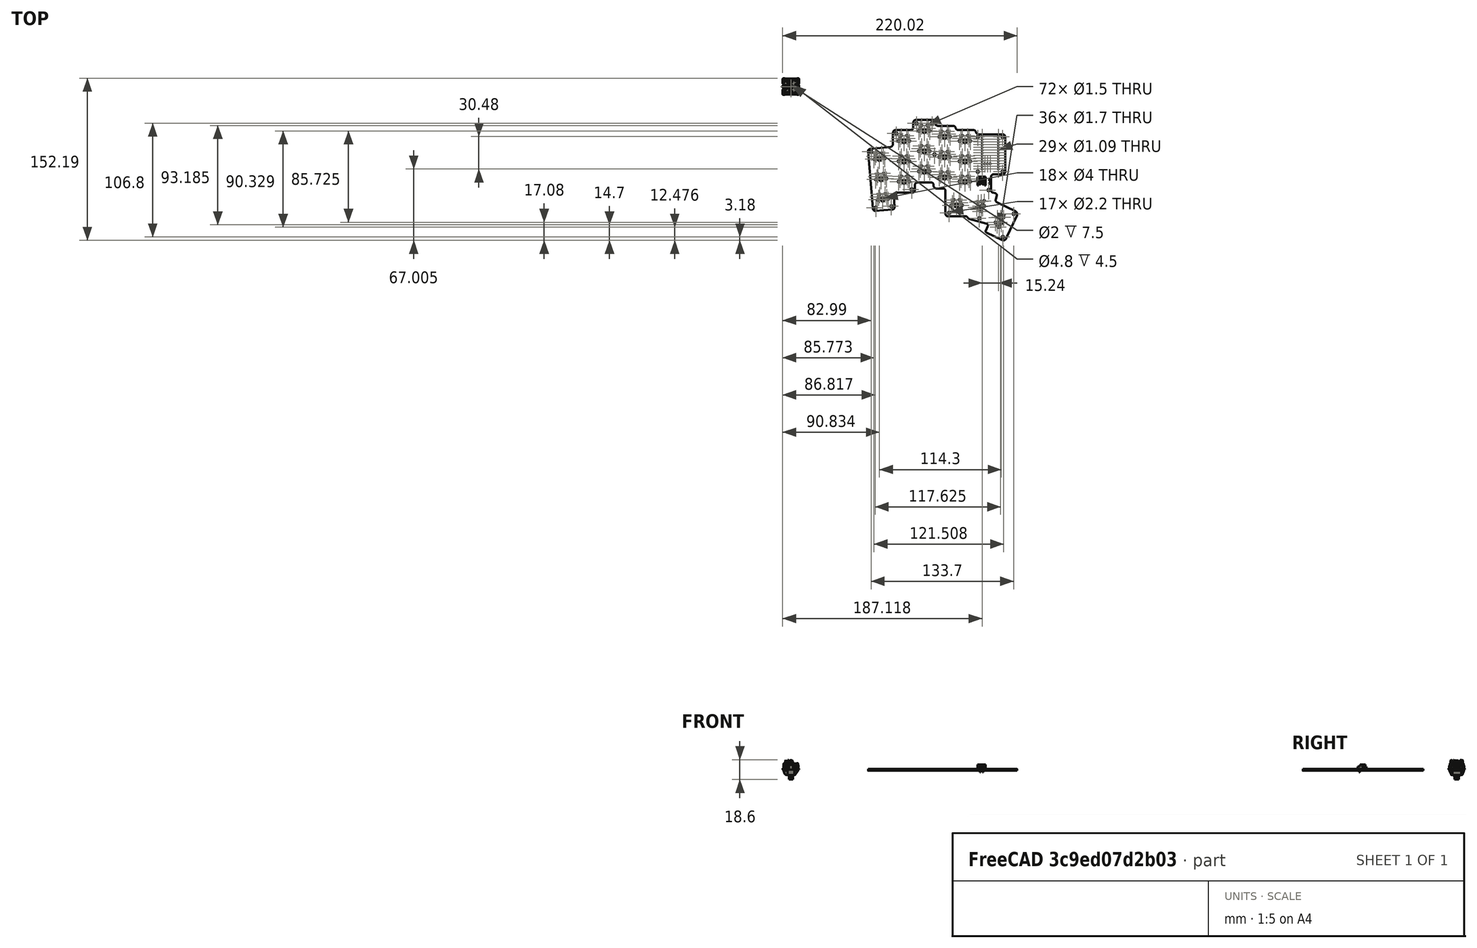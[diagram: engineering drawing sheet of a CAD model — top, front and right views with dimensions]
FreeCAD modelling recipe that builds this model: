
FCSTD DOCUMENT  (FreeCAD 0.19R24267 +99 (Git))
Label: Diom-35SP
License: All rights reserved
LicenseURL: http://en.wikipedia.org/wiki/All_rights_reserved
objects: App::Link×17, Part::Feature×12, App::Part×5, PartDesign::CoordinateSystem×1, Sketcher::SketchObject×1
note: 14 computed .brp shape members not serialized (recipe doc carries the construction recipe); baked Part::Feature solids carry a one-line shape summary decoded from their .brp

FEATURE [PartDesign::CoordinateSystem] Local_CS_b1ef
  AttacherType = Attacher::AttachEngine3D
FEATURE [Part::Feature] Pcb_b1ef
  shape: bbox 139.9 x 113.1 x 1.6 mm, 239 faces (baked)
FEATURE [Sketcher::SketchObject] PCB_Sketch_b1ef
  FullyConstrained = false
  sketch-geometry (61):
    g0: LineSegment StartX=188.042 StartY=-84.455 StartZ=0 EndX=188.019 EndY=-97 EndZ=0
    g1: LineSegment StartX=93.6625 StartY=-56.3562 StartZ=0 EndX=74.7 EndY=-58.2 EndZ=0
    g2: LineSegment StartX=77.1188 StartY=-114.019 StartZ=0 EndX=72.6 EndY=-60.6 EndZ=0
    g3: LineSegment StartX=135.604 StartY=-34.1313 StartZ=0 EndX=135.604 EndY=-33.3375 EndZ=0
    g4: LineSegment StartX=190.423 StartY=-82.042 StartZ=0 EndX=198.882 EndY=-82.042 EndZ=0
    g5: LineSegment StartX=145.256 StartY=-119.412 StartZ=0 EndX=145.256 EndY=-97.282 EndZ=0
    g6: LineSegment StartX=189.8 StartY=-99.3 StartZ=0 EndX=192.1 EndY=-99.9 EndZ=0
    g7: LineSegment StartX=198.882 StartY=-44.45 StartZ=0 EndX=176.213 EndY=-44.45 EndZ=0
    g8: LineSegment StartX=202.4 StartY=-141.9 StartZ=0 EndX=212.306 EndY=-120.437 EndZ=0
    g9: LineSegment StartX=112.713 StartY=-40.4813 StartZ=0 EndX=98.425 EndY=-40.4813 EndZ=0
    g10: LineSegment StartX=119 StartY=-89.7 StartZ=0 EndX=131.762 EndY=-89.6937 EndZ=0
    g11: LineSegment StartX=167.6 StartY=-124 StartZ=0 EndX=183.822 EndY=-128.377 EndZ=0
    g12: LineSegment StartX=183.515 StartY=-136.779 StartZ=0 EndX=198.209 EndY=-143.805 EndZ=0
    g13: LineSegment StartX=210.805 StartY=-116.739 StartZ=0 EndX=193.6 EndY=-108.4 EndZ=0
    g14: LineSegment StartX=116.619 StartY=-92.0812 StartZ=0 EndX=116.6 EndY=-96.8375 EndZ=0
    g15: LineSegment StartX=95.25 StartY=-115.094 StartZ=0 EndX=79.5 EndY=-116.4 EndZ=0
    g16: LineSegment StartX=136.525 StartY=-95.25 StartZ=0 EndX=142.875 EndY=-95.25 EndZ=0
    g17: LineSegment StartX=114.219 StartY=-99.2188 StartZ=0 EndX=99.2188 EndY=-99.2188 EndZ=0
    g18: LineSegment StartX=115.094 StartY=-33.3375 StartZ=0 EndX=115.094 EndY=-38.1 EndZ=0
    g19: LineSegment StartX=201.263 StartY=-46.8312 StartZ=0 EndX=201.263 EndY=-79.6607 EndZ=0
    g20: LineSegment StartX=192.408 StartY=-105.58 StartZ=0 EndX=193.4 EndY=-102.2 EndZ=0
    g21: LineSegment StartX=96.0438 StartY=-42.8625 StartZ=0 EndX=96.0438 EndY=-53.975 EndZ=0
    g22: LineSegment StartX=171.45 StartY=-40.4813 StartZ=0 EndX=157.162 EndY=-40.4813 EndZ=0
    g23: LineSegment StartX=134.144 StartY=-92.075 StartZ=0 EndX=134.144 EndY=-92.8688 EndZ=0
    g24: LineSegment StartX=96.8375 StartY=-101.6 StartZ=0 EndX=97.6312 EndY=-112.713 EndZ=0
    g25: LineSegment StartX=133.223 StartY=-30.9563 StartZ=0 EndX=117.475 EndY=-30.9562 EndZ=0
    g26: LineSegment StartX=152.4 StartY=-36.5125 StartZ=0 EndX=138.004 EndY=-36.5125 EndZ=0
    g27: LineSegment StartX=184.893 StartY=-130.9 StartZ=0 EndX=183.134 EndY=-134.62 EndZ=0
    g28: LineSegment StartX=147.637 StartY=-121.444 StartZ=0 EndX=164.2 EndY=-121.444 EndZ=0
    g29: ArcOfCircle CenterX=133.223 CenterY=-33.3375 CenterZ=0 NormalX=0 NormalY=0 NormalZ=-1 AngleXU=1.5708 Radius=2.38125 StartAngle=0 EndAngle=1.5708
    g30: ArcOfCircle CenterX=209.705 CenterY=-119.339 CenterZ=0 NormalX=0 NormalY=0 NormalZ=-1 AngleXU=1.97104 Radius=2.82312 StartAngle=0 EndAngle=1.57002
    g31: ArcOfCircle CenterX=131.762 CenterY=-92.075 CenterZ=0 NormalX=0 NormalY=0 NormalZ=-1 AngleXU=1.5708 Radius=2.38125 StartAngle=0 EndAngle=1.5708
    g32: ArcOfCircle CenterX=79.5 CenterY=-114.019 CenterZ=0 NormalX=0 NormalY=0 NormalZ=-1 AngleXU=-1.57079 Radius=2.38125 StartAngle=0 EndAngle=1.57079
    g33: ArcOfCircle CenterX=136.525 CenterY=-92.8687 CenterZ=0 NormalX=0 NormalY=0 NormalZ=-1 AngleXU=-1.5708 Radius=2.38125 StartAngle=0 EndAngle=1.5708
    g34: ArcOfCircle CenterX=119 CenterY=-92.0813 CenterZ=0 NormalX=0 NormalY=0 NormalZ=-1 AngleXU=3.25477e-08 Radius=2.38125 StartAngle=0 EndAngle=1.5708
    g35: ArcOfCircle CenterX=164.177 CenterY=-123.544 CenterZ=0 NormalX=0 NormalY=0 NormalZ=-1 AngleXU=1.5819 Radius=2.10035 StartAngle=0 EndAngle=1.14618
    g36: ArcOfCircle CenterX=152.4 CenterY=-38.9238 CenterZ=0 NormalX=0 NormalY=0 NormalZ=-1 AngleXU=1.5708 Radius=2.41126 StartAngle=0 EndAngle=1.41285
    g37: ArcOfCircle CenterX=95.25 CenterY=-112.712 CenterZ=0 NormalX=0 NormalY=0 NormalZ=-1 AngleXU=-3.14159 Radius=2.38125 StartAngle=0 EndAngle=1.5708
    g38: ArcOfCircle CenterX=74.8692 CenterY=-60.4668 CenterZ=0 NormalX=0 NormalY=0 NormalZ=-1 AngleXU=-0.0586452 Radius=2.27308 StartAngle=0 EndAngle=1.55495
    g39: ArcOfCircle CenterX=190.423 CenterY=-84.4235 CenterZ=0 NormalX=0 NormalY=0 NormalZ=-1 AngleXU=-0.0132458 Radius=2.38146 StartAngle=0 EndAngle=1.58404
    g40: ArcOfCircle CenterX=98.425 CenterY=-42.8625 CenterZ=0 NormalX=0 NormalY=0 NormalZ=-1 AngleXU=1.46634e-06 Radius=2.38125 StartAngle=0 EndAngle=1.57079
    g41: ArcOfCircle CenterX=171.45 CenterY=-42.8925 CenterZ=0 NormalX=0 NormalY=0 NormalZ=-1 AngleXU=1.5708 Radius=2.41126 StartAngle=0 EndAngle=1.41285
    g42: ArcOfCircle CenterX=194.58 CenterY=-106.324 CenterZ=0 NormalX=0 NormalY=0 NormalZ=-1 AngleXU=-1.12967 Radius=2.29598 StartAngle=0 EndAngle=1.45965
    g43: ArcOfCircle CenterX=112.712 CenterY=-38.1 CenterZ=0 NormalX=0 NormalY=0 NormalZ=-1 AngleXU=-3.14159 Radius=2.38125 StartAngle=0 EndAngle=1.5708
    g44: ArcOfCircle CenterX=176.212 CenterY=-42.0177 CenterZ=0 NormalX=0 NormalY=0 NormalZ=-1 AngleXU=-1.5708 Radius=2.43226 StartAngle=0 EndAngle=1.36564
    g45: ArcOfCircle CenterX=183.441 CenterY=-130.028 CenterZ=0 NormalX=0 NormalY=0 NormalZ=-1 AngleXU=1.79759 Radius=1.69439 StartAngle=0 EndAngle=1.88442
    g46: ArcOfCircle CenterX=191.6 CenterY=-101.7 CenterZ=0 NormalX=0 NormalY=0 NormalZ=-1 AngleXU=1.84174 Radius=1.86815 StartAngle=0 EndAngle=1.5708
    g47: ArcOfCircle CenterX=184.703 CenterY=-135.456 CenterZ=0 NormalX=0 NormalY=0 NormalZ=-1 AngleXU=-0.839035 Radius=1.7779 StartAngle=0 EndAngle=1.32873
    g48: ArcOfCircle CenterX=198.882 CenterY=-46.8313 CenterZ=0 NormalX=0 NormalY=0 NormalZ=-1 AngleXU=1.57082 Radius=2.3813 StartAngle=0 EndAngle=1.57075
    g49: ArcOfCircle CenterX=114.219 CenterY=-96.8375 CenterZ=0 NormalX=0 NormalY=0 NormalZ=-1 AngleXU=-3.14159 Radius=2.38125 StartAngle=0 EndAngle=1.5708
    g50: ArcOfCircle CenterX=199.473 CenterY=-141.024 CenterZ=0 NormalX=0 NormalY=0 NormalZ=-1 AngleXU=-2.85068 Radius=3.05515 StartAngle=0 EndAngle=1.70651
    g51: ArcOfCircle CenterX=147.638 CenterY=-119.032 CenterZ=0 NormalX=0 NormalY=0 NormalZ=-1 AngleXU=-1.5708 Radius=2.41126 StartAngle=0 EndAngle=1.41285
    g52: ArcOfCircle CenterX=99.2188 CenterY=-101.6 CenterZ=0 NormalX=0 NormalY=0 NormalZ=-1 AngleXU=3.25477e-08 Radius=2.38125 StartAngle=0 EndAngle=1.5708
    g53: ArcOfCircle CenterX=198.882 CenterY=-79.6607 CenterZ=0 NormalX=0 NormalY=0 NormalZ=-1 AngleXU=-3.14157 Radius=2.3813 StartAngle=0 EndAngle=1.57075
    g54: ArcOfCircle CenterX=168.281 CenterY=-121.699 CenterZ=0 NormalX=0 NormalY=0 NormalZ=-1 AngleXU=-1.28308 Radius=2.39977 StartAngle=0 EndAngle=0.852742
    g55: ArcOfCircle CenterX=190.257 CenterY=-97.1066 CenterZ=0 NormalX=0 NormalY=0 NormalZ=-1 AngleXU=-1.36524 Radius=2.2406 StartAngle=0 EndAngle=1.41282
    g56: ArcOfCircle CenterX=93.0579 CenterY=-53.3704 CenterZ=0 NormalX=0 NormalY=0 NormalZ=-1 AngleXU=-2.94181 Radius=3.04641 StartAngle=0 EndAngle=1.17124
    g57: ArcOfCircle CenterX=138.004 CenterY=-34.1124 CenterZ=0 NormalX=0 NormalY=0 NormalZ=-1 AngleXU=-1.5708 Radius=2.40007 StartAngle=0 EndAngle=1.56295
    g58: ArcOfCircle CenterX=157.162 CenterY=-38.049 CenterZ=0 NormalX=0 NormalY=0 NormalZ=-1 AngleXU=-1.5708 Radius=2.43226 StartAngle=0 EndAngle=1.36564
    g59: ArcOfCircle CenterX=142.875 CenterY=-97.6613 CenterZ=0 NormalX=0 NormalY=0 NormalZ=-1 AngleXU=1.5708 Radius=2.41126 StartAngle=0 EndAngle=1.41285
    g60: ArcOfCircle CenterX=117.475 CenterY=-33.3375 CenterZ=0 NormalX=0 NormalY=0 NormalZ=-1 AngleXU=1.46634e-06 Radius=2.38125 StartAngle=0 EndAngle=1.57079
  constraints (61):
    c: Coincident(g2,g38)
    c: Coincident(g1,g38)
    c: Coincident(g2,g32)
    c: Coincident(g32,g15)
    c: Coincident(g1,g56)
    c: Coincident(g37,g15)
    c: Coincident(g21,g56)
    c: Coincident(g40,g21)
    c: Coincident(g52,g24)
    c: Coincident(g24,g37)
    c: Coincident(g9,g40)
    c: Coincident(g52,g17)
    c: Coincident(g43,g9)
    c: Coincident(g49,g17)
    c: Coincident(g43,g18)
    c: Coincident(g60,g18)
    c: Coincident(g49,g14)
    c: Coincident(g14,g34)
    c: Coincident(g25,g60)
    c: Coincident(g10,g34)
    c: Coincident(g10,g31)
    c: Coincident(g25,g29)
    c: Coincident(g23,g33)
    c: Coincident(g23,g31)
    c: Coincident(g3,g57)
    c: Coincident(g29,g3)
    c: Coincident(g33,g16)
    c: Coincident(g26,g57)
    c: Coincident(g16,g59)
    c: Coincident(g5,g51)
    c: Coincident(g5,g59)
    c: Coincident(g28,g51)
    c: Coincident(g36,g26)
    c: Coincident(g36,g58)
    c: Coincident(g22,g58)
    c: Coincident(g35,g28)
    c: Coincident(g54,g35)
    c: Coincident(g11,g54)
    c: Coincident(g22,g41)
    c: Coincident(g44,g41)
    c: Coincident(g7,g44)
    c: Coincident(g27,g47)
    c: Coincident(g47,g12)
    c: Coincident(g45,g11)
    c: Coincident(g45,g27)
    c: Coincident(g0,g55)
    c: Coincident(g0,g39)
    c: Coincident(g6,g55)
    c: Coincident(g4,g39)
    c: Coincident(g46,g6)
    c: Coincident(g42,g20)
    c: Coincident(g46,g20)
    c: Coincident(g42,g13)
    c: Coincident(g12,g50)
    c: Coincident(g53,g4)
    c: Coincident(g48,g7)
    c: Coincident(g53,g19)
    c: Coincident(g19,g48)
    c: Coincident(g50,g8)
    c: Coincident(g30,g13)
    c: Coincident(g8,g30)
FEATURE [Part::Feature] Part__Feature  label="MX_DOWN"
  Placement = pos=(0.307087,0.307087,-0.34252) rot=(0,0,1;0rad)
  shape: bbox 15.61 x 15.61 x 12.51 mm, 297 faces (baked)
FEATURE [Part::Feature] Part__Feature001  label="MX_UP"
  Placement = pos=(0.307087,0.307087,-5.74252) rot=(0,0,1;0rad)
  shape: bbox 14.7 x 14.7 x 10.05 mm, 224 faces (baked)
FEATURE [Part::Feature] Part__Feature002  label="UP_MX"
  Placement = pos=(3.15709,0.307087,0.45748) rot=(0.57735,0.57735,-0.57735;4.18879rad)
  shape: bbox 5.703 x 8.903 x 12.4 mm, 73 faces (baked)
FEATURE [Part::Feature] Part__Feature003  label="MX_PIN"
  Placement = pos=(-2.59291,4.00709,8.45748) rot=(0.57735,-0.57735,0.57735;4.18879rad)
  shape: bbox 3.204 x 9.819 x 13.17 mm, 187 faces, 2 solids (baked)
FEATURE [Part::Feature] Part__Feature004  label="MX_SPRING"
  Placement = pos=(0.307087,0.307087,6.75748) rot=(0,0,1;0rad)
  shape: bbox 3.277 x 3.277 x 11.32 mm, 14 faces (baked)
FEATURE [Part::Feature] Part__Feature005  label="MX_CLICK"
  Placement = pos=(-2.14619,-4.14291,2.15226) rot=(-1,0,0;1.5708rad)
  shape: bbox 6.856 x 8.91 x 3.858 mm, 123 faces (baked)
FEATURE [App::Part] asm_mx_asm_PCB_v2  label="MX2_asm_mx_asm_PCB v2_509173e2f2d2"
  Group = -> [Part__Feature,Part__Feature001,Part__Feature002,Part__Feature003,Part__Feature004,Part__Feature005]
  Origin = -> Origin008
  Placement = pos=(106.612,-50.55,5) rot=(-0.707107,0.707107,0;3.14159rad)
FEATURE [App::Link] MX2_asm_mx_asm_PCB_v2_509173e2f2d2_ln_  label="MX16_asm_mx_asm_PCB v2_61c1af00679b"
  LinkPlacement = pos=(155.984,-110.875,5) rot=(-0.707107,0.707107,0;3.14159rad)
  LinkedObject = -> asm_mx_asm_PCB_v2
  Placement = pos=(155.984,-110.875,5) rot=(-0.707107,0.707107,0;3.14159rad)
FEATURE [App::Link] MX2_asm_mx_asm_PCB_v2_509173e2f2d2_ln_001  label="MX7_asm_mx_asm_PCB v2_8bcd4c388b4b"
  LinkPlacement = pos=(106.612,-69.6,5) rot=(-0.707107,0.707107,0;3.14159rad)
  LinkedObject = -> asm_mx_asm_PCB_v2
  Placement = pos=(106.612,-69.6,5) rot=(-0.707107,0.707107,0;3.14159rad)
FEATURE [App::Link] MX2_asm_mx_asm_PCB_v2_509173e2f2d2_ln_002  label="MX14_asm_mx_asm_PCB v2_522a68924cf1"
  LinkPlacement = pos=(144.713,-84.6813,5) rot=(-0.707107,0.707107,0;3.14159rad)
  LinkedObject = -> asm_mx_asm_PCB_v2
  Placement = pos=(144.713,-84.6813,5) rot=(-0.707107,0.707107,0;3.14159rad)
FEATURE [App::Link] MX2_asm_mx_asm_PCB_v2_509173e2f2d2_ln_003  label="MX1_asm_mx_asm_PCB v2_e2a4cddd902f"
  LinkPlacement = pos=(83.571,-67.1979,5) rot=(0.737277,-0.67559,0;3.14159rad)
  LinkedObject = -> asm_mx_asm_PCB_v2
  Placement = pos=(83.571,-67.1979,5) rot=(0.737277,-0.67559,0;3.14159rad)
FEATURE [Part::Feature] Shape  label="J1_JST_S2B_EH_347234a4d46b"
  Placement = pos=(177.82,-91.0515,0) rot=(0,0,1;0rad)
  shape: bbox 7.5 x 8.2 x 7.4 mm, 98 faces (baked)
FEATURE [App::Link] MX2_asm_mx_asm_PCB_v2_509173e2f2d2_ln_004  label="MX6_asm_mx_asm_PCB v2_e2ed95cca693"
  LinkPlacement = pos=(85.1585,-86.2479,5) rot=(0.737277,-0.67559,0;3.14159rad)
  LinkedObject = -> asm_mx_asm_PCB_v2
  Placement = pos=(85.1585,-86.2479,5) rot=(0.737277,-0.67559,0;3.14159rad)
FEATURE [App::Link] MX2_asm_mx_asm_PCB_v2_509173e2f2d2_ln_005  label="MX5_asm_mx_asm_PCB v2_8ad58eddd87c"
  LinkPlacement = pos=(163.762,-50.55,5) rot=(-0.707107,0.707107,0;3.14159rad)
  LinkedObject = -> asm_mx_asm_PCB_v2
  Placement = pos=(163.762,-50.55,5) rot=(-0.707107,0.707107,0;3.14159rad)
FEATURE [App::Link] MX2_asm_mx_asm_PCB_v2_509173e2f2d2_ln_006  label="MX9_asm_mx_asm_PCB v2_586121fcf8e0"
  LinkPlacement = pos=(144.713,-65.6312,5) rot=(-0.707107,0.707107,0;3.14159rad)
  LinkedObject = -> asm_mx_asm_PCB_v2
  Placement = pos=(144.713,-65.6312,5) rot=(-0.707107,0.707107,0;3.14159rad)
FEATURE [App::Link] MX2_asm_mx_asm_PCB_v2_509173e2f2d2_ln_007  label="MX17_asm_mx_asm_PCB v2_aae10874eaa3"
  LinkPlacement = pos=(180.004,-111.613,5.5) rot=(0.991445,-0.130526,0;3.14159rad)
  LinkedObject = -> asm_mx_asm_PCB_v2
  Placement = pos=(180.004,-111.613,5.5) rot=(0.991445,-0.130526,0;3.14159rad)
FEATURE [App::Link] MX2_asm_mx_asm_PCB_v2_509173e2f2d2_ln_008  label="MX3_asm_mx_asm_PCB v2_7a4bacda9721"
  LinkPlacement = pos=(125.662,-41.025,5) rot=(-0.707107,0.707107,0;3.14159rad)
  LinkedObject = -> asm_mx_asm_PCB_v2
  Placement = pos=(125.662,-41.025,5) rot=(-0.707107,0.707107,0;3.14159rad)
FEATURE [App::Link] MX2_asm_mx_asm_PCB_v2_509173e2f2d2_ln_009  label="MX13_asm_mx_asm_PCB v2_06f37e21ca1b"
  LinkPlacement = pos=(125.662,-79.125,5) rot=(-0.707107,0.707107,0;3.14159rad)
  LinkedObject = -> asm_mx_asm_PCB_v2
  Placement = pos=(125.662,-79.125,5) rot=(-0.707107,0.707107,0;3.14159rad)
FEATURE [App::Link] MX2_asm_mx_asm_PCB_v2_509173e2f2d2_ln_010  label="MX15_asm_mx_asm_PCB v2_3662dd4e56b2"
  LinkPlacement = pos=(163.762,-88.65,5) rot=(-0.707107,0.707107,0;3.14159rad)
  LinkedObject = -> asm_mx_asm_PCB_v2
  Placement = pos=(163.762,-88.65,5) rot=(-0.707107,0.707107,0;3.14159rad)
FEATURE [App::Link] MX2_asm_mx_asm_PCB_v2_509173e2f2d2_ln_011  label="MX12_asm_mx_asm_PCB v2_11247fadff60"
  LinkPlacement = pos=(106.612,-88.65,5) rot=(-0.707107,0.707107,0;3.14159rad)
  LinkedObject = -> asm_mx_asm_PCB_v2
  Placement = pos=(106.612,-88.65,5) rot=(-0.707107,0.707107,0;3.14159rad)
FEATURE [App::Link] MX2_asm_mx_asm_PCB_v2_509173e2f2d2_ln_012  label="MX18_asm_mx_asm_PCB v2_43c1ebdc5ceb"
  LinkPlacement = pos=(197.523,-126.668,5.5) rot=(0.976296,-0.21644,0;3.14159rad)
  LinkedObject = -> asm_mx_asm_PCB_v2
  Placement = pos=(197.523,-126.668,5.5) rot=(0.976296,-0.21644,0;3.14159rad)
FEATURE [App::Link] MX2_asm_mx_asm_PCB_v2_509173e2f2d2_ln_013  label="MX4_asm_mx_asm_PCB v2_0a8aad10b025"
  LinkPlacement = pos=(144.713,-46.5812,5) rot=(-0.707107,0.707107,0;3.14159rad)
  LinkedObject = -> asm_mx_asm_PCB_v2
  Placement = pos=(144.713,-46.5812,5) rot=(-0.707107,0.707107,0;3.14159rad)
FEATURE [App::Link] MX2_asm_mx_asm_PCB_v2_509173e2f2d2_ln_014  label="MX10_asm_mx_asm_PCB v2_0672621efad5"
  LinkPlacement = pos=(163.762,-69.6,5) rot=(-0.707107,0.707107,0;3.14159rad)
  LinkedObject = -> asm_mx_asm_PCB_v2
  Placement = pos=(163.762,-69.6,5) rot=(-0.707107,0.707107,0;3.14159rad)
FEATURE [App::Link] MX2_asm_mx_asm_PCB_v2_509173e2f2d2_ln_015  label="MX8_asm_mx_asm_PCB v2_ee36b2acd693"
  LinkPlacement = pos=(125.662,-60.075,5) rot=(-0.707107,0.707107,0;3.14159rad)
  LinkedObject = -> asm_mx_asm_PCB_v2
  Placement = pos=(125.662,-60.075,5) rot=(-0.707107,0.707107,0;3.14159rad)
FEATURE [App::Link] MX2_asm_mx_asm_PCB_v2_509173e2f2d2_ln_016  label="MX11_asm_mx_asm_PCB v2_ac296a31bdc0"
  LinkPlacement = pos=(86.746,-105.298,5) rot=(0.737277,-0.67559,0;3.14159rad)
  LinkedObject = -> asm_mx_asm_PCB_v2
  Placement = pos=(86.746,-105.298,5) rot=(0.737277,-0.67559,0;3.14159rad)
FEATURE [App::Part] Top_b1ef
  Group = -> [asm_mx_asm_PCB_v2,MX2_asm_mx_asm_PCB_v2_509173e2f2d2_ln_,MX2_asm_mx_asm_PCB_v2_509173e2f2d2_ln_001,MX2_asm_mx_asm_PCB_v2_509173e2f2d2_ln_002,MX2_asm_mx_asm_PCB_v2_509173e2f2d2_ln_003,Shape,MX2_asm_mx_asm_PCB_v2_509173e2f2d2_ln_004,MX2_asm_mx_asm_PCB_v2_509173e2f2d2_ln_005,MX2_asm_mx_asm_PCB_v2_509173e2f2d2_ln_006,MX2_asm_mx_asm_PCB_v2_509173e2f2d2_ln_007,MX2_asm_mx_asm_PCB_v2_509173e2f2d2_ln_008,+8 more]
  Origin = -> Origin003
FEATURE [App::Part] Step_Models_b1ef
  Group = -> [Top_b1ef]
  Origin = -> Origin002
FEATURE [Part::Feature] pads_area037001  label="topPads_b1ef"
  Placement = pos=(0,0,0.02) rot=(0,0,1;0rad)
  shape: bbox 119.8 x 95.38 x 2e-07 mm, 105 faces, 0 solids (baked)
FEATURE [Part::Feature] tracks_area001  label="topTracks_b1ef"
  Placement = pos=(0,0,0.01) rot=(0,0,1;0rad)
  shape: bbox 115.7 x 90.43 x 2e-07 mm, 36 faces, 0 solids (baked)
FEATURE [Part::Feature] pads_area037040001  label="botPads_b1ef"
  Placement = pos=(0,0,-1.62) rot=(0,0,1;0rad)
  shape: bbox 119.8 x 95.38 x 2e-07 mm, 112 faces, 0 solids (baked)
FEATURE [Part::Feature] tracks_area002001  label="botTracks_b1ef"
  Placement = pos=(0,0,-1.61) rot=(0,0,1;0rad)
  shape: bbox 14.71 x 28.49 x 2e-07 mm, 3 faces, 0 solids (baked)
FEATURE [App::Part] Board_Geoms_b1ef
  Group = -> [Local_CS_b1ef,Pcb_b1ef,PCB_Sketch_b1ef,pads_area037001,tracks_area001,pads_area037040001,tracks_area002001]
  Origin = -> Origin
FEATURE [App::Part] Board_b1ef  label="Diom-35SP_PCB-noSilk-black"
  Group = -> [Board_Geoms_b1ef,Step_Models_b1ef]
  Origin = -> Origin001
